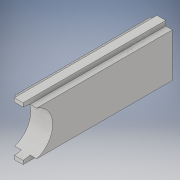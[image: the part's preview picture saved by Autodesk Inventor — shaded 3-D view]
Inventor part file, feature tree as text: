
AUTODESK INVENTOR PART (.ipt)
format: ipt  version: 2018 (Build 220112000, 112)  size: 120,320 bytes
history: native  units: in
note: dims shown in document units (in); Inventor stores cm internally (conversion verified against a paired STEP export)
features: extrude x2, sketch x2
ambient origin geometry x8: Origin, YZ Plane, XZ Plane, XY Plane, X Axis, Y Axis, Z Axis, Center Point
bodies: Solid1 (feature_tree)
feature tree (4):
  extrude  "Extrusion1"  Depth=1.0in
  extrude  "Extrusion2"  Depth=0.11in
  sketch  "Sketch1"  dims[d0=0.5in d1=1.0in]
  sketch  "Sketch2"  dims[d2=0.2in d3=0.11in d4=0.15in d5=0.2in d6=0.11in d7=0.15in d8=3.25in d9=0.0in d10=1.05in d11=3.25in d12=0.0in]
